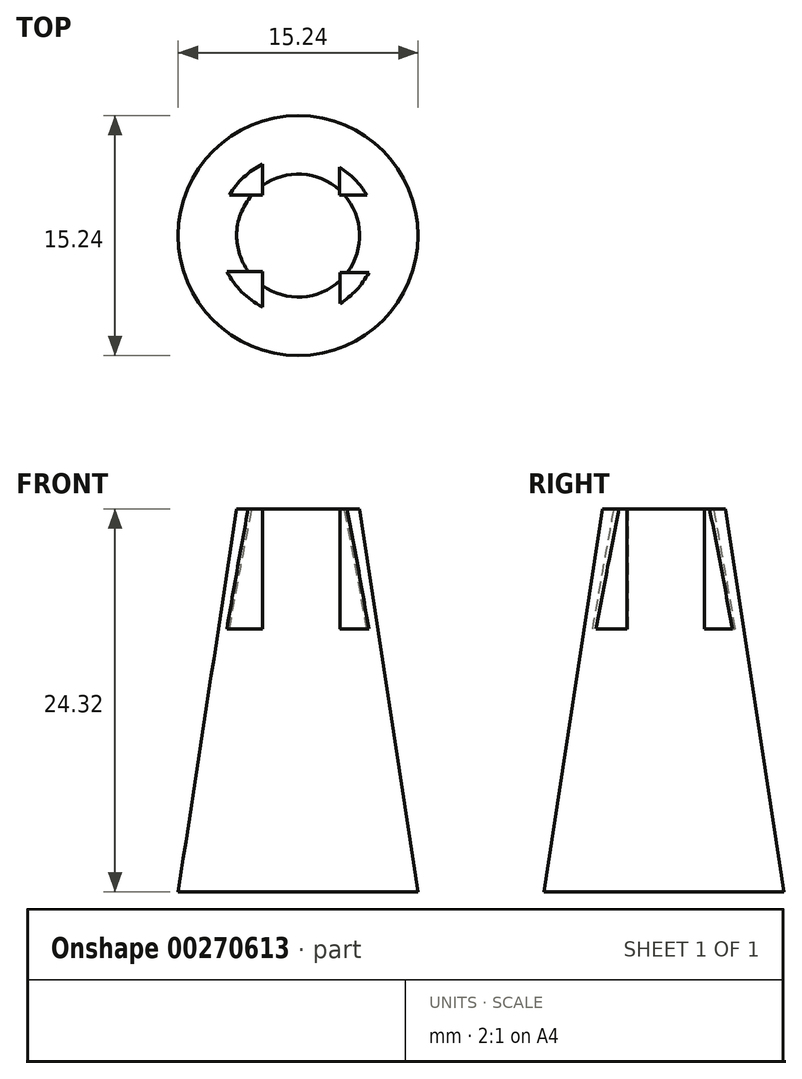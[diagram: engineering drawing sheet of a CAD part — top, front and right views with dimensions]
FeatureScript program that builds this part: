
annotation { "Feature Type Name" : "Feature", "Feature Type Description" : "" }
export const myFeature = defineFeature(function(context is Context, id is Id, definition is map)
    precondition{}
    {
        {
            var Q0;
            Q0=qCreatedBy(makeId("Front.planeOp"),FACE);
            var sketch = newSketch(context, id + "F0", { "sketchPlane" : qUnion([Q0])});
            skLineSegment(sketch, "E0", {"start": v(0, 0) * mm, "end": v(0, 24.32) * mm});
            skLineSegment(sketch, "E1", {"start": v(0, 24.32) * mm, "end": v(3.9, 24.32) * mm});
            skLineSegment(sketch, "E2", {"start": v(3.9, 24.32) * mm, "end": v(7.62, 0) * mm});
            skLineSegment(sketch, "E3", {"start": v(0, 0) * mm, "end": v(7.62, 0) * mm});
            skSolve(sketch);
        }
        {
            var Q0;
            Q0 = qSketchRegion(id + "F0", true);
            var Q1;
            Q1=sQuery(id+"F0.wireOp",EDGE,"E0");
            revolve(context, id + "F1", {"entities" : qUnion([Q0]), "axis" : qUnion([Q1]), "revolveType" : RevolveType.FULL});
        }
        {
            var Q0;
            Q0=makeQuery(id+"F1.opRevolve","SWEPT_FACE",FACE,{"disambiguationData":[OSD([sQuery(id+"F0.wireOp",EDGE,"E1")])]});
            cPlane(context, id + "F2", {"entities" : qUnion([Q0]), "cplaneType" : CPlaneType.OFFSET, "offset" : 0 * mm, "width" : 152.4 * mm, "height" : 152.4 * mm});
        }
        {
            var Q0;
            Q0=qCreatedBy(id+"F2.planeOp",FACE);
            var sketch = newSketch(context, id + "F3", { "sketchPlane" : qUnion([Q0])});
            skLineSegment(sketch, "E4.bottom", {"start": v(4.79, -5) * mm, "end": v(2.66, -5) * mm});
            skLineSegment(sketch, "E4.top", {"start": v(4.79, -2.35) * mm, "end": v(2.66, -2.35) * mm});
            skLineSegment(sketch, "E4.left", {"start": v(4.79, -5) * mm, "end": v(4.79, -2.35) * mm});
            skLineSegment(sketch, "E4.right", {"start": v(2.66, -5) * mm, "end": v(2.66, -2.35) * mm});
            skPoint(sketch, "E4.middle", {"position": v(3.72, -3.67) * mm});
            skLineSegment(sketch, "E5.bottom", {"start": v(2.62, 2.57) * mm, "end": v(4.95, 2.57) * mm});
            skLineSegment(sketch, "E5.top", {"start": v(2.62, 5) * mm, "end": v(4.95, 5) * mm});
            skLineSegment(sketch, "E5.left", {"start": v(2.62, 2.57) * mm, "end": v(2.62, 5) * mm});
            skLineSegment(sketch, "E5.right", {"start": v(4.95, 2.57) * mm, "end": v(4.95, 5) * mm});
            skPoint(sketch, "E5.middle", {"position": v(3.79, 3.78) * mm});
            skLineSegment(sketch, "E6.bottom", {"start": v(-2.27, -2.27) * mm, "end": v(-6.05, -2.27) * mm});
            skLineSegment(sketch, "E6.top", {"start": v(-2.27, -5.28) * mm, "end": v(-6.05, -5.28) * mm});
            skLineSegment(sketch, "E6.left", {"start": v(-2.27, -2.27) * mm, "end": v(-2.27, -5.28) * mm});
            skLineSegment(sketch, "E6.right", {"start": v(-6.05, -2.27) * mm, "end": v(-6.05, -5.28) * mm});
            skPoint(sketch, "E6.middle", {"position": v(-4.16, -3.78) * mm});
            skLineSegment(sketch, "E7.bottom", {"start": v(-2.27, 2.57) * mm, "end": v(-6.18, 2.57) * mm});
            skLineSegment(sketch, "E7.top", {"start": v(-2.27, 5.01) * mm, "end": v(-6.18, 5.01) * mm});
            skLineSegment(sketch, "E7.left", {"start": v(-2.27, 2.57) * mm, "end": v(-2.27, 5.01) * mm});
            skLineSegment(sketch, "E7.right", {"start": v(-6.18, 2.57) * mm, "end": v(-6.18, 5.01) * mm});
            skPoint(sketch, "E7.middle", {"position": v(-4.23, 3.8) * mm});
            skSolve(sketch);
        }
        {
            var Q0;
            Q0 = qSketchRegion(id + "F3", true);
            extrude(context, id + "F4", {"entities" : qUnion([Q0]), "operationType" : NewBodyOperationType.REMOVE, "oppositeDirection" : true, "depth" : 7.62 * mm});
        }
    });
